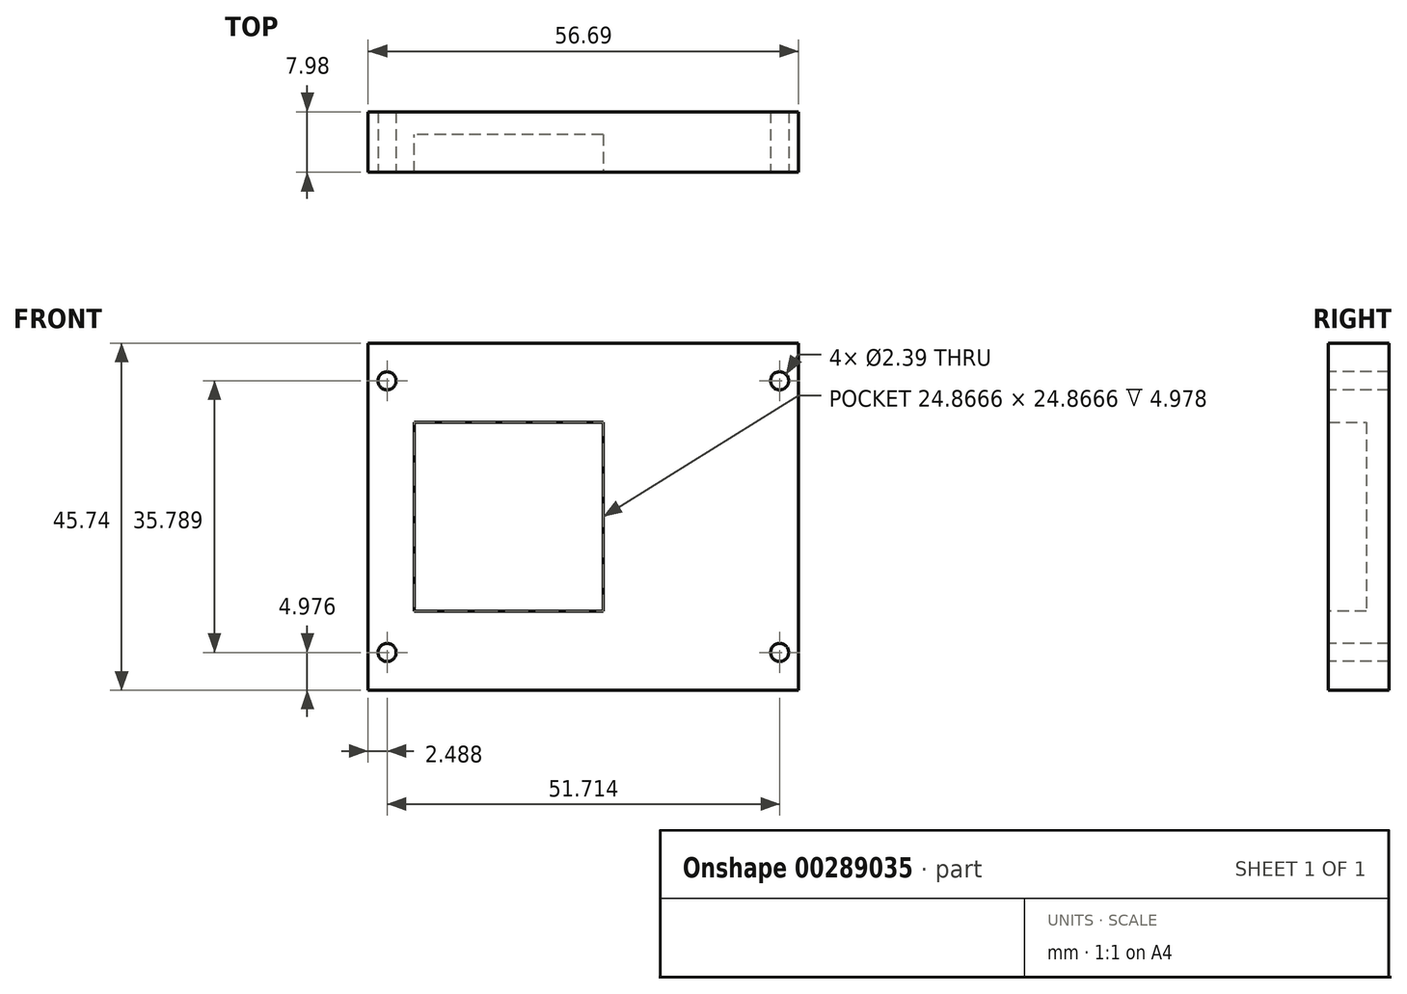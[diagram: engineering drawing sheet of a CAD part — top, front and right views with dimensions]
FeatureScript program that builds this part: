
annotation { "Feature Type Name" : "Feature", "Feature Type Description" : "" }
export const myFeature = defineFeature(function(context is Context, id is Id, definition is map)
    precondition{}
    {
        {
            var Q0;
            Q0=qCreatedBy(makeId("Front.planeOp"),FACE);
            var sketch = newSketch(context, id + "F0", { "sketchPlane" : qUnion([Q0])});
            skLineSegment(sketch, "E0.bottom", {"start": v(-46.01, 25.88) * mm, "end": v(10.68, 25.88) * mm});
            skLineSegment(sketch, "E0.top", {"start": v(-46.01, -19.86) * mm, "end": v(10.68, -19.86) * mm});
            skLineSegment(sketch, "E0.left", {"start": v(-46.01, 25.88) * mm, "end": v(-46.01, -19.86) * mm});
            skLineSegment(sketch, "E0.right", {"start": v(10.68, 25.88) * mm, "end": v(10.68, -19.86) * mm});
            skSolve(sketch);
        }
        {
            var Q0;
            Q0=makeQuery(id+"F0.imprint","IMPRINT",FACE,{"disambiguationData":[TD([[makeQuery(id+"F0.imprint","IMPRINT",EDGE,{"derivedFrom":sQuery(id+"F0.wireOp",EDGE,"E0.bottom")}),-1.0]])]});
            extrude(context, id + "F1", {"entities" : qUnion([Q0]), "depth" : 7.98 * mm});
        }
        {
            var Q0;
            Q0=makeQuery(id+"F1.opExtrude","CAP_FACE",FACE,{"disambiguationData":[OSD([sQuery(id+"F0.wireOp",EDGE,"E0.bottom"),sQuery(id+"F0.wireOp",EDGE,"E0.top"),sQuery(id+"F0.wireOp",EDGE,"E0.left"),sQuery(id+"F0.wireOp",EDGE,"E0.right")])],"isStart":false});
            var sketch = newSketch(context, id + "F2", { "sketchPlane" : qUnion([Q0])});
            skPoint(sketch, "E1", {"position": v(-43.52, 20.9) * mm});
            skPoint(sketch, "E2", {"position": v(8.2, 20.9) * mm});
            skPoint(sketch, "E3", {"position": v(8.2, -14.88) * mm});
            skPoint(sketch, "E4", {"position": v(-43.52, -14.88) * mm});
            skSolve(sketch);
        }
        {
            var Q0;
            Q0=sQuery(id+"F2.wireOp",VERTEX,"E1");
            var Q1;
            Q1=sQuery(id+"F2.wireOp",VERTEX,"E2");
            var Q2;
            Q2=sQuery(id+"F2.wireOp",VERTEX,"E3");
            var Q3;
            Q3=sQuery(id+"F2.wireOp",VERTEX,"E4");
            var Q4;
            Q4=makeQuery(id+"F1.opExtrude","SWEPT_BODY",BODY,{"disambiguationData":[OSD([sQuery(id+"F0.wireOp",EDGE,"E0.bottom"),sQuery(id+"F0.wireOp",EDGE,"E0.top"),sQuery(id+"F0.wireOp",EDGE,"E0.left"),sQuery(id+"F0.wireOp",EDGE,"E0.right")])]});
            hole(context, id + "F3", {"style" : HoleStyle.SIMPLE, "endStyle" : HoleEndStyle.THROUGH, "holeDiameter" : 2.4 * mm, "tappedDepth" : 12.7 * mm, "tapClearance" : 3, "locations" : qUnion([Q0, Q1, Q2, Q3]), "scope" : qUnion([Q4])});
        }
        {
            var Q0;
            Q0=makeQuery(id+"F1.opExtrude","CAP_FACE",FACE,{"disambiguationData":[OSD([sQuery(id+"F0.wireOp",EDGE,"E0.bottom"),sQuery(id+"F0.wireOp",EDGE,"E0.top"),sQuery(id+"F0.wireOp",EDGE,"E0.left"),sQuery(id+"F0.wireOp",EDGE,"E0.right")])],"isStart":false});
            var sketch = newSketch(context, id + "F4", { "sketchPlane" : qUnion([Q0])});
            skLineSegment(sketch, "E5.bottom", {"start": v(-39.94, 15.44) * mm, "end": v(-15.07, 15.44) * mm});
            skLineSegment(sketch, "E5.top", {"start": v(-39.94, -9.42) * mm, "end": v(-15.07, -9.42) * mm});
            skLineSegment(sketch, "E5.left", {"start": v(-39.94, 15.44) * mm, "end": v(-39.94, -9.42) * mm});
            skLineSegment(sketch, "E5.right", {"start": v(-15.07, 15.44) * mm, "end": v(-15.07, -9.42) * mm});
            skSolve(sketch);
        }
        {
            var Q0;
            Q0=makeQuery(id+"F4.imprint","IMPRINT",FACE,{"disambiguationData":[TD([[makeQuery(id+"F4.imprint","IMPRINT",EDGE,{"derivedFrom":sQuery(id+"F4.wireOp",EDGE,"E5.bottom")}),-1.0]])]});
            extrude(context, id + "F5", {"entities" : qUnion([Q0]), "operationType" : NewBodyOperationType.REMOVE, "oppositeDirection" : true, "depth" : 4.98 * mm, "hasDraft" : true, "draftAngle" : 0 * degree, "draftPullDirection" : true});
        }
    });
